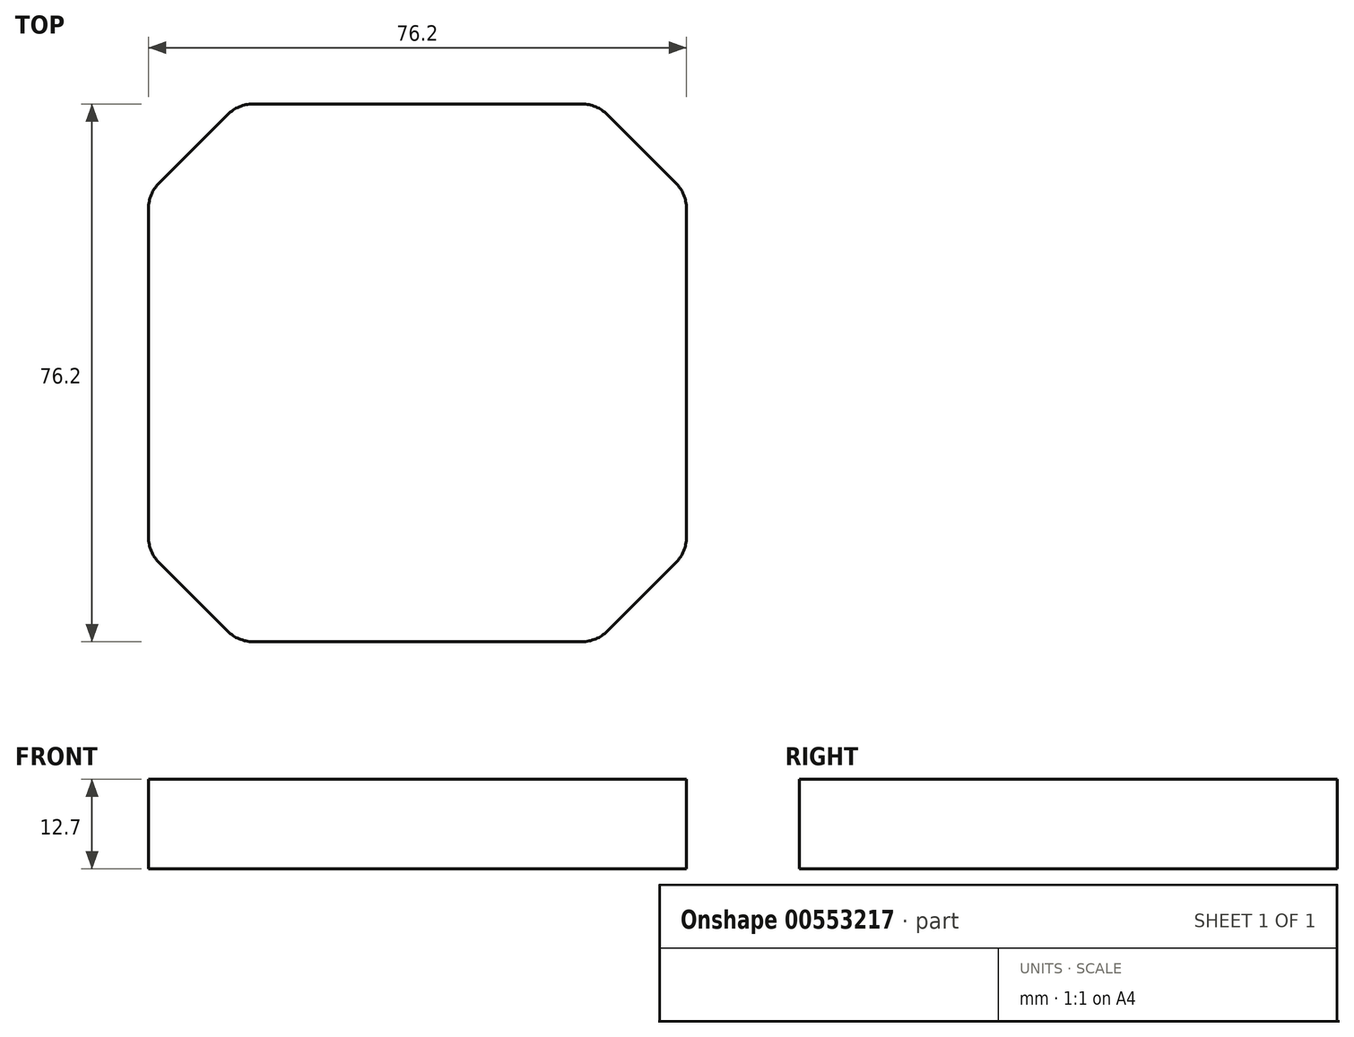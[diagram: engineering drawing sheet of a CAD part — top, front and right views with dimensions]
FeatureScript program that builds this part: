
annotation { "Feature Type Name" : "Feature", "Feature Type Description" : "" }
export const myFeature = defineFeature(function(context is Context, id is Id, definition is map)
    precondition{}
    {
        {
            var Q0;
            Q0=qCreatedBy(makeId("Top.planeOp"),FACE);
            var sketch = newSketch(context, id + "F0", { "sketchPlane" : qUnion([Q0])});
            skLineSegment(sketch, "E0.bottom", {"start": v(38.1, 38.1) * mm, "end": v(-38.1, 38.1) * mm});
            skLineSegment(sketch, "E0.top", {"start": v(38.1, -38.1) * mm, "end": v(-38.1, -38.1) * mm});
            skLineSegment(sketch, "E0.left", {"start": v(38.1, 38.1) * mm, "end": v(38.1, -38.1) * mm});
            skLineSegment(sketch, "E0.right", {"start": v(-38.1, 38.1) * mm, "end": v(-38.1, -38.1) * mm});
            skPoint(sketch, "E0.middle", {"position": v(0, 0) * mm});
            skSolve(sketch);
        }
        {
            var Q0;
            Q0 = qSketchRegion(id + "F0", true);
            extrude(context, id + "F1", {"entities" : qUnion([Q0]), "depth" : 12.7 * mm, "offsetDistance" : 25.4 * mm});
        }
        {
            var Q0;
            Q0=makeQuery(id+"F1.opExtrude","SWEPT_EDGE",EDGE,{"disambiguationData":[OSD([sQuery(id+"F0.wireOp",EDGE,"E0.top"),sQuery(id+"F0.wireOp",EDGE,"E0.right")])]});
            var Q1;
            Q1=makeQuery(id+"F1.opExtrude","SWEPT_EDGE",EDGE,{"disambiguationData":[OSD([sQuery(id+"F0.wireOp",EDGE,"E0.top"),sQuery(id+"F0.wireOp",EDGE,"E0.left")])]});
            var Q2;
            Q2=makeQuery(id+"F1.opExtrude","SWEPT_EDGE",EDGE,{"disambiguationData":[OSD([sQuery(id+"F0.wireOp",EDGE,"E0.bottom"),sQuery(id+"F0.wireOp",EDGE,"E0.right")])]});
            var Q3;
            Q3=makeQuery(id+"F1.opExtrude","SWEPT_EDGE",EDGE,{"disambiguationData":[OSD([sQuery(id+"F0.wireOp",EDGE,"E0.bottom"),sQuery(id+"F0.wireOp",EDGE,"E0.left")])]});
            chamfer(context, id + "F2", {"entities" : qUnion([Q0, Q1, Q2, Q3]), "width" : 12.7 * mm, "tangentPropagation" : true});
        }
        {
            var Q0;
            {var subQ0=sQuery(id+"F0.wireOp",EDGE,"E0.top");Q0=makeQuery(id+"F2.opChamfer","BLEND_EDGE",EDGE,{"blendedFrom":[makeQuery(id+"F1.opExtrude","SWEPT_EDGE",EDGE,{"disambiguationData":[OSD([subQ0,sQuery(id+"F0.wireOp",EDGE,"E0.left")])]}),makeQuery(id+"F1.opExtrude","SWEPT_FACE",FACE,{"disambiguationData":[OSD([subQ0])]})],"blendedInto":[makeQuery(id+"F1.opExtrude","SWEPT_FACE",FACE,{"disambiguationData":[OSD([subQ0])]})]});}
            var Q1;
            {var subQ0=sQuery(id+"F0.wireOp",EDGE,"E0.left");Q1=makeQuery(id+"F2.opChamfer","BLEND_EDGE",EDGE,{"blendedFrom":[makeQuery(id+"F1.opExtrude","SWEPT_EDGE",EDGE,{"disambiguationData":[OSD([sQuery(id+"F0.wireOp",EDGE,"E0.top"),subQ0])]}),makeQuery(id+"F1.opExtrude","SWEPT_FACE",FACE,{"disambiguationData":[OSD([subQ0])]})],"blendedInto":[makeQuery(id+"F1.opExtrude","SWEPT_FACE",FACE,{"disambiguationData":[OSD([subQ0])]})]});}
            var Q2;
            {var subQ0=sQuery(id+"F0.wireOp",EDGE,"E0.left");Q2=makeQuery(id+"F2.opChamfer","BLEND_EDGE",EDGE,{"blendedFrom":[makeQuery(id+"F1.opExtrude","SWEPT_EDGE",EDGE,{"disambiguationData":[OSD([sQuery(id+"F0.wireOp",EDGE,"E0.bottom"),subQ0])]}),makeQuery(id+"F1.opExtrude","SWEPT_FACE",FACE,{"disambiguationData":[OSD([subQ0])]})],"blendedInto":[makeQuery(id+"F1.opExtrude","SWEPT_FACE",FACE,{"disambiguationData":[OSD([subQ0])]})]});}
            var Q3;
            {var subQ0=sQuery(id+"F0.wireOp",EDGE,"E0.bottom");Q3=makeQuery(id+"F2.opChamfer","BLEND_EDGE",EDGE,{"blendedFrom":[makeQuery(id+"F1.opExtrude","SWEPT_EDGE",EDGE,{"disambiguationData":[OSD([subQ0,sQuery(id+"F0.wireOp",EDGE,"E0.left")])]}),makeQuery(id+"F1.opExtrude","SWEPT_FACE",FACE,{"disambiguationData":[OSD([subQ0])]})],"blendedInto":[makeQuery(id+"F1.opExtrude","SWEPT_FACE",FACE,{"disambiguationData":[OSD([subQ0])]})]});}
            var Q4;
            {var subQ0=sQuery(id+"F0.wireOp",EDGE,"E0.bottom");Q4=makeQuery(id+"F2.opChamfer","BLEND_EDGE",EDGE,{"blendedFrom":[makeQuery(id+"F1.opExtrude","SWEPT_EDGE",EDGE,{"disambiguationData":[OSD([subQ0,sQuery(id+"F0.wireOp",EDGE,"E0.right")])]}),makeQuery(id+"F1.opExtrude","SWEPT_FACE",FACE,{"disambiguationData":[OSD([subQ0])]})],"blendedInto":[makeQuery(id+"F1.opExtrude","SWEPT_FACE",FACE,{"disambiguationData":[OSD([subQ0])]})]});}
            var Q5;
            {var subQ0=sQuery(id+"F0.wireOp",EDGE,"E0.right");Q5=makeQuery(id+"F2.opChamfer","BLEND_EDGE",EDGE,{"blendedFrom":[makeQuery(id+"F1.opExtrude","SWEPT_EDGE",EDGE,{"disambiguationData":[OSD([sQuery(id+"F0.wireOp",EDGE,"E0.bottom"),subQ0])]}),makeQuery(id+"F1.opExtrude","SWEPT_FACE",FACE,{"disambiguationData":[OSD([subQ0])]})],"blendedInto":[makeQuery(id+"F1.opExtrude","SWEPT_FACE",FACE,{"disambiguationData":[OSD([subQ0])]})]});}
            var Q6;
            {var subQ0=sQuery(id+"F0.wireOp",EDGE,"E0.right");Q6=makeQuery(id+"F2.opChamfer","BLEND_EDGE",EDGE,{"blendedFrom":[makeQuery(id+"F1.opExtrude","SWEPT_EDGE",EDGE,{"disambiguationData":[OSD([sQuery(id+"F0.wireOp",EDGE,"E0.top"),subQ0])]}),makeQuery(id+"F1.opExtrude","SWEPT_FACE",FACE,{"disambiguationData":[OSD([subQ0])]})],"blendedInto":[makeQuery(id+"F1.opExtrude","SWEPT_FACE",FACE,{"disambiguationData":[OSD([subQ0])]})]});}
            var Q7;
            {var subQ0=sQuery(id+"F0.wireOp",EDGE,"E0.top");Q7=makeQuery(id+"F2.opChamfer","BLEND_EDGE",EDGE,{"blendedFrom":[makeQuery(id+"F1.opExtrude","SWEPT_EDGE",EDGE,{"disambiguationData":[OSD([subQ0,sQuery(id+"F0.wireOp",EDGE,"E0.right")])]}),makeQuery(id+"F1.opExtrude","SWEPT_FACE",FACE,{"disambiguationData":[OSD([subQ0])]})],"blendedInto":[makeQuery(id+"F1.opExtrude","SWEPT_FACE",FACE,{"disambiguationData":[OSD([subQ0])]})]});}
            fillet(context, id + "F3", {"entities" : qUnion([Q0, Q1, Q2, Q3, Q4, Q5, Q6, Q7]), "radius" : 5.08 * mm, "tangentPropagation" : true, "allowEdgeOverflow" : false});
        }
    });
